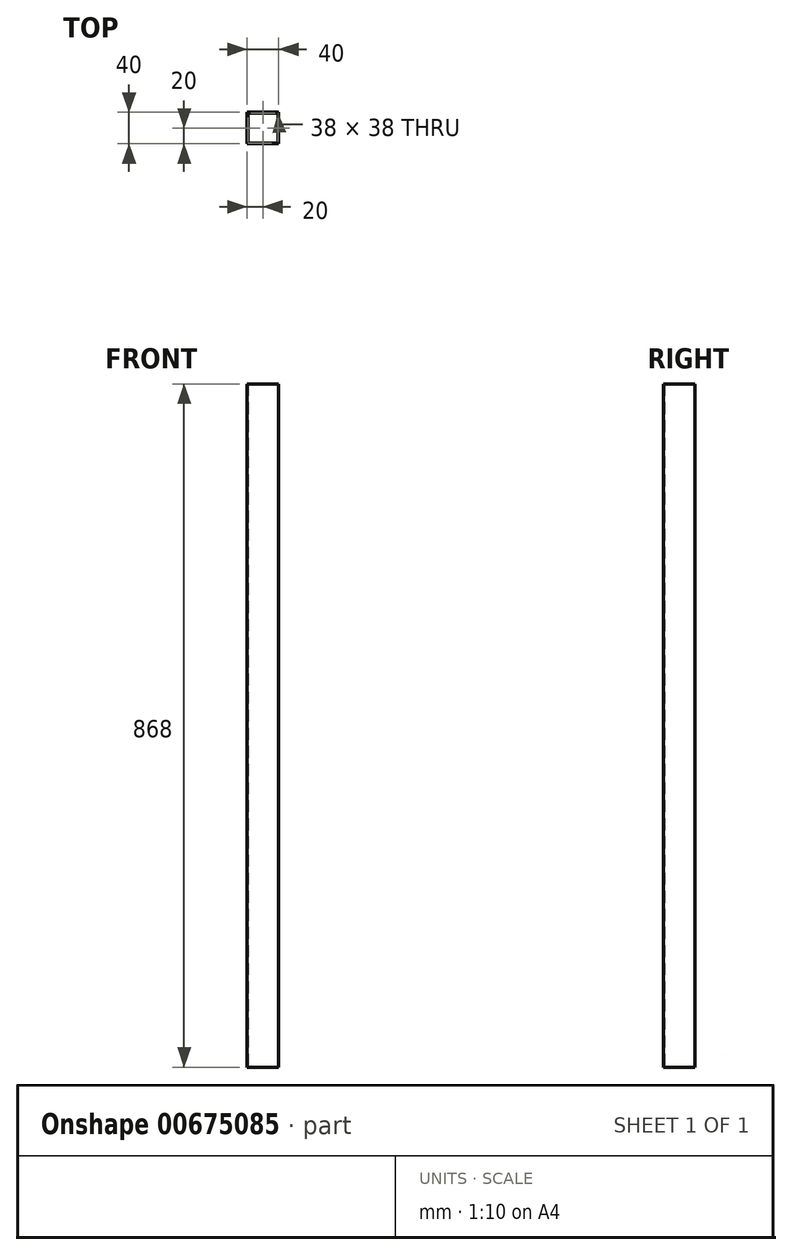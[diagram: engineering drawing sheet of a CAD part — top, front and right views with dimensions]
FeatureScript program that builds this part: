
annotation { "Feature Type Name" : "Feature", "Feature Type Description" : "" }
export const myFeature = defineFeature(function(context is Context, id is Id, definition is map)
    precondition{}
    {
        {
            var Q0;
            Q0=qCreatedBy(makeId("Top.planeOp"),FACE);
            var sketch = newSketch(context, id + "F0", { "sketchPlane" : qUnion([Q0])});
            skLineSegment(sketch, "E0.bottom", {"start": v(19, 19) * mm, "end": v(-19, 19) * mm});
            skLineSegment(sketch, "E0.top", {"start": v(19, -19) * mm, "end": v(-19, -19) * mm});
            skLineSegment(sketch, "E0.left", {"start": v(19, 19) * mm, "end": v(19, -19) * mm});
            skLineSegment(sketch, "E0.right", {"start": v(-19, 19) * mm, "end": v(-19, -19) * mm});
            skPoint(sketch, "E0.middle", {"position": v(0, 0) * mm});
            skLineSegment(sketch, "E1.bottom", {"start": v(20, 20) * mm, "end": v(-20, 20) * mm});
            skLineSegment(sketch, "E1.top", {"start": v(20, -20) * mm, "end": v(-20, -20) * mm});
            skLineSegment(sketch, "E1.left", {"start": v(20, 20) * mm, "end": v(20, -20) * mm});
            skLineSegment(sketch, "E1.right", {"start": v(-20, 20) * mm, "end": v(-20, -20) * mm});
            skSolve(sketch);
        }
        {
            var Q0;
            Q0=makeQuery(id+"F0.imprint","IMPRINT",FACE,{"disambiguationData":[TD([[makeQuery(id+"F0.imprint","IMPRINT",EDGE,{"derivedFrom":sQuery(id+"F0.wireOp",EDGE,"E0.bottom")}),-1.0]])]});
            extrude(context, id + "F1", {"entities" : qUnion([Q0]), "depth" : 868 * mm, "offsetDistance" : 25 * mm});
        }
    });
